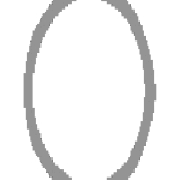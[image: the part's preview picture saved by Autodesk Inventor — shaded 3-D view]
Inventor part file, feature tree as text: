
AUTODESK INVENTOR PART (.ipt)
format: ipt  version: 2021 (Build 250183000, 183)  size: 109,056 bytes
history: native  units: in
note: dims shown in document units (in); Inventor stores cm internally (conversion verified against a paired STEP export)
features: other x4, sketch x3, plane x1
ambient origin geometry x8: Origin, YZ Plane, XZ Plane, XY Plane, X Axis, Y Axis, Z Axis, Center Point
bodies: Solid1 (feature_tree), Body (feature_tree)
feature tree (8):
  other  "Driven Length"
  other  "Frame Generator"
  other  "Start Plane"
  other  "End Plane"
  sketch  "Sketch"  dims[d2=22.0in d4=-0.0in d5=22.0in d6=0.12in d7=0.0in d8=90.0deg d9=22.0in]
  sketch  "Sketch2"  dims[d0=1.0in]
  plane  "Work Plane3"
  sketch  "Sketch3"  dims[d1=0.065in]
